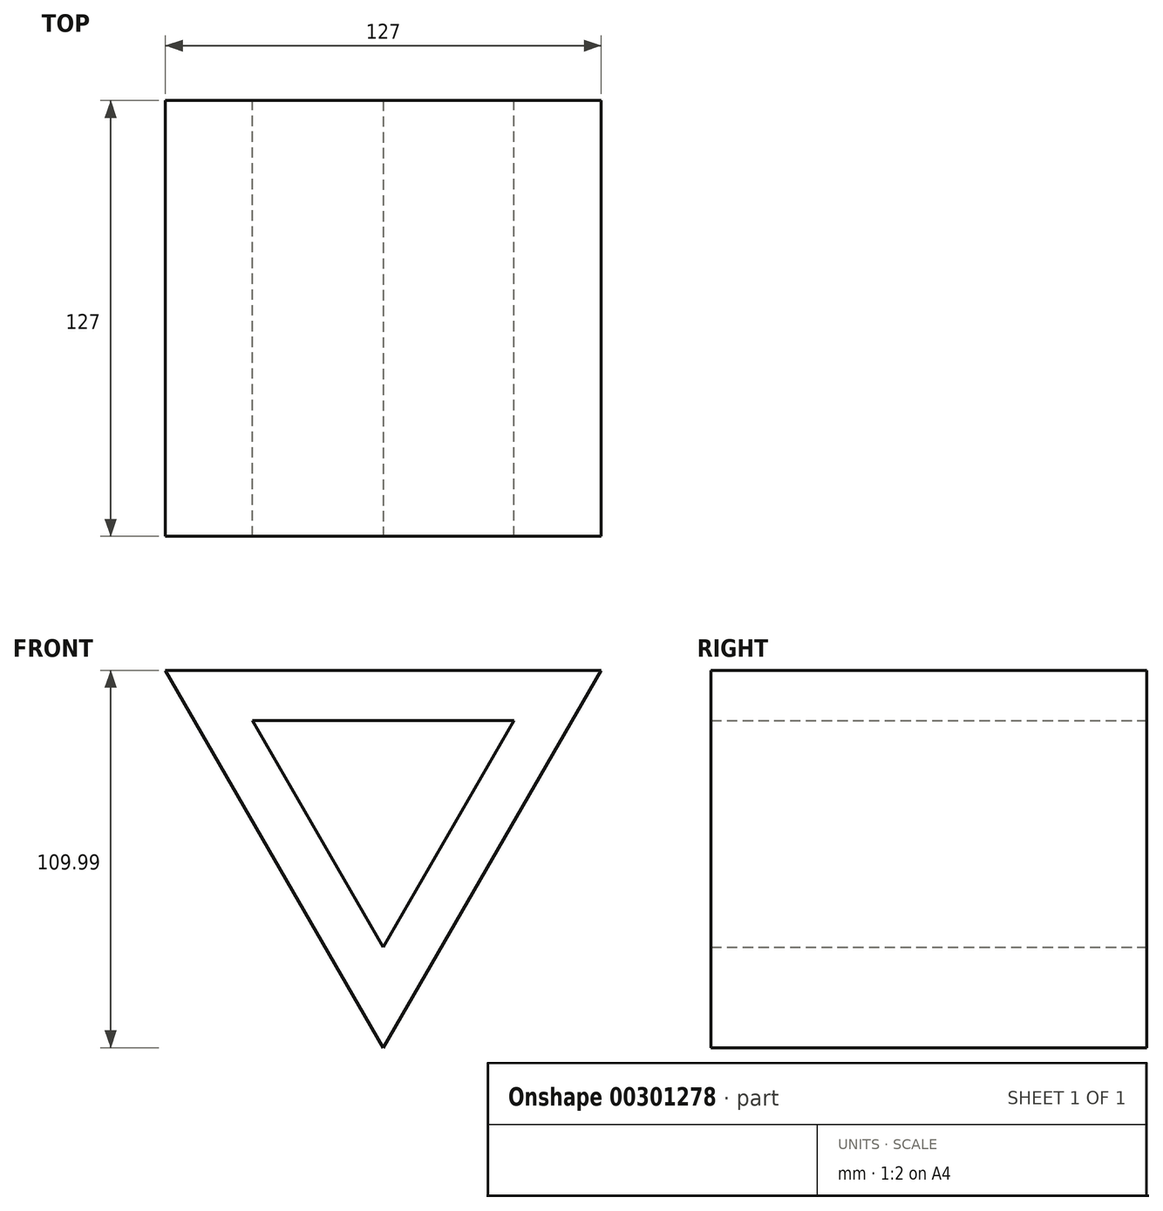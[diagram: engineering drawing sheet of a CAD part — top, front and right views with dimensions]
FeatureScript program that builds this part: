
annotation { "Feature Type Name" : "Feature", "Feature Type Description" : "" }
export const myFeature = defineFeature(function(context is Context, id is Id, definition is map)
    precondition{}
    {
        {
            var Q0;
            Q0=qCreatedBy(makeId("Front.planeOp"),FACE);
            var sketch = newSketch(context, id + "F0", { "sketchPlane" : qUnion([Q0])});
            skLineSegment(sketch, "E0", {"start": v(-63.5, 0) * mm, "end": v(63.5, 0) * mm});
            skLineSegment(sketch, "E1", {"start": v(63.5, 0) * mm, "end": v(0, -109.99) * mm});
            skLineSegment(sketch, "E2", {"start": v(0, -109.99) * mm, "end": v(-63.5, 0) * mm});
            skSolve(sketch);
        }
        {
            var Q0;
            Q0=qCreatedBy(makeId("Front.planeOp"),FACE);
            cPlane(context, id + "F1", {"entities" : qUnion([Q0]), "cplaneType" : CPlaneType.OFFSET, "offset" : 127 * mm, "oppositeDirection" : true, "width" : 152.4 * mm, "height" : 152.4 * mm});
        }
        {
            var Q0;
            Q0=qCreatedBy(id+"F1.planeOp",FACE);
            var sketch = newSketch(context, id + "F2", { "sketchPlane" : qUnion([Q0])});
            skLineSegment(sketch, "E3", {"start": v(-38.1, -14.68) * mm, "end": v(38.1, -14.68) * mm});
            skLineSegment(sketch, "E4", {"start": v(38.1, -14.68) * mm, "end": v(0, -80.67) * mm});
            skLineSegment(sketch, "E5", {"start": v(0, -80.67) * mm, "end": v(-38.1, -14.68) * mm});
            skSolve(sketch);
        }
        {
            var Q0;
            Q0=makeQuery(id+"F0.imprint","IMPRINT",FACE,{"disambiguationData":[TD([[makeQuery(id+"F0.imprint","IMPRINT",EDGE,{"derivedFrom":sQuery(id+"F0.wireOp",EDGE,"E0")}),-1.0]])]});
            extrude(context, id + "F3", {"entities" : qUnion([Q0]), "oppositeDirection" : true, "depth" : 127 * mm});
        }
        {
            var Q0;
            Q0=makeQuery(id+"F2.imprint","IMPRINT",FACE,{"disambiguationData":[TD([[makeQuery(id+"F2.imprint","IMPRINT",EDGE,{"derivedFrom":sQuery(id+"F2.wireOp",EDGE,"E3")}),-1.0]])]});
            extrude(context, id + "F4", {"entities" : qUnion([Q0]), "operationType" : NewBodyOperationType.REMOVE, "depth" : 127 * mm});
        }
    });
